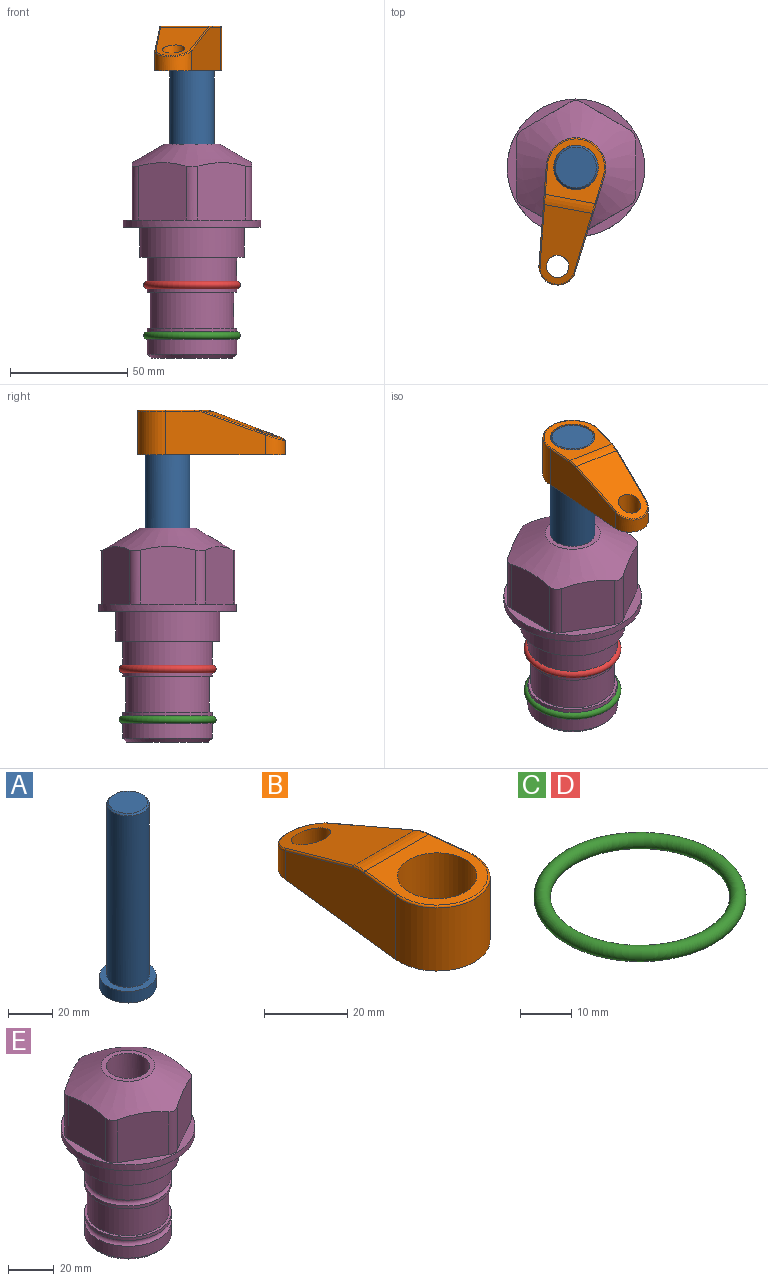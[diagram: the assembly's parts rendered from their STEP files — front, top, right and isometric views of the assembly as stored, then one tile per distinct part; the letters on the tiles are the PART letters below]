
ASSEMBLY  parts=5 mates=3
PART A: 6 faces, bbox 25.4x25.4x101.6 mm
  f0: plane 17.46x17.46mm, normal (0,0,1), area 239.5mm2, adj f5
  f1: plane 25.4x25.4mm, normal (0,0,-1), area 506.7mm2, adj f2
  f2: cylinder r=12.7mm len=25.4mm, axis (0,0,1), area 506.7mm2, adj f1,f3
  f3: plane 25.4x25.4mm, normal (0,0,1), area 221.7mm2, adj f2,f4
  f4: cylinder r=9.53mm len=94.46mm, axis (0,0,1), area 5653mm2, adj f3,f5
  f5: cone r=8.73mm half-angle=45deg, axis (0,0,-1), area 64.4mm2, adj f0,f4
PART B: 44 faces, bbox 27.5x64.5x19.1 mm
  f0: plane 2.3x0.95mm, normal (0,0,-1), area 1mm2, adj f25,f30,f34
  f1: plane 63.5x25.4mm, normal (0,0,-1), area 561.7mm2, adj f2,f3,f4,f5,f6,f7,f19,f20
  f2: cylinder r=12.7mm len=25.4mm, axis (0,0,-1), area 792.2mm2, adj f1,f3,f5,f13
  f3: plane 42.33x18.54mm, normal (0.99,0.11,0), area 647mm2, adj f1,f2,f4,f11,f12,f14
  f4: cylinder r=7.94mm len=15.78mm, axis (0,0,-1), area 158.6mm2, adj f1,f3,f5,f16
  f5: plane 42.33x18.54mm, normal (-0.99,0.11,0), area 647mm2, adj f1,f2,f4,f15,f17,f18
  f6: cylinder r=9.53mm len=19.05mm, axis (0,0,-1), area 1140.1mm2, adj f1,f8
  f7: cylinder r=4.76mm len=10.98mm, axis (0,0,-1), area 276.1mm2, adj f1,f9
  f8: plane 25.83x24.38mm, normal (0,0,1), area 262.2mm2, adj f6,f10,f11,f13,f15
  f9: plane 32.49x20.55mm, normal (0,0.34,0.94), area 489.9mm2, adj f7,f10,f14,f16,f18
  f10: cylinder r=12.7mm len=21.49mm, axis (-1,0,0), area 93.2mm2, adj f8,f9,f12,f17
  f11: cylinder r=0.51mm len=12.34mm, axis (0.11,-0.99,0), area 9.9mm2, adj f3,f8,f12,f13
  f12: bspline ~7.62x1.64mm, area 3.5mm2, adj f3,f10,f11,f14
  f13: torus R=12.19mm, axis (0,0,1), area 33.6mm2, adj f2,f8,f11,f15
  f14: cylinder r=0.51mm len=26.01mm, axis (0.1,-0.93,0.34), area 21.6mm2, adj f3,f9,f12,f16
  f15: cylinder r=0.51mm len=12.34mm, axis (0.11,0.99,0), area 9.9mm2, adj f5,f8,f13,f17
  f16: bspline ~15.78x7.05mm, area 15.7mm2, adj f4,f9,f14,f18
  f17: bspline ~7.62x1.64mm, area 3.5mm2, adj f5,f10,f15,f18
  f18: cylinder r=0.51mm len=26.01mm, axis (0.1,0.93,-0.34), area 21.6mm2, adj f5,f9,f16,f17
  f19: plane 21.6x14.29mm, normal (-0.99,-0.11,0), area 242.6mm2, adj f1,f26,f28,f34,f36,f38
  f20: plane 21.6x14.29mm, normal (0.99,-0.11,0), area 242.6mm2, adj f1,f27,f29,f37,f39,f41
  f21: cylinder r=12.7mm len=14.29mm, axis (0,0,-1), area 173.2mm2, adj f1,f26,f27,f30,f31,f33
  f22: cylinder r=7.94mm len=7.63mm, axis (0,0,-1), area 53.8mm2, adj f1,f28,f29,f42
  f23: plane 2.3x0.95mm, normal (0,0,-1), area 1mm2, adj f25,f33,f37
  f24: plane 17.94x12.32mm, normal (0,-0.34,-0.94), area 191.2mm2, adj f25,f38,f41,f42
  f25: cylinder r=9.53mm len=12.93mm, axis (-1,0,0), area 37.5mm2, adj f0,f23,f24,f31,f36,f39
  f26: cylinder r=1.59mm len=14.29mm, axis (0,0,-1), area 49mm2, adj f1,f19,f21,f32
  f27: cylinder r=1.59mm len=14.29mm, axis (0,0,-1), area 49mm2, adj f1,f20,f21,f35
  f28: cylinder r=1.59mm len=7.28mm, axis (0,0,-1), area 22.1mm2, adj f1,f19,f22,f40
  f29: cylinder r=1.59mm len=7.28mm, axis (0,0,-1), area 22.1mm2, adj f1,f20,f22,f43
  f30: torus R=14.29mm, axis (0,0,1), area 5.8mm2, adj f0,f21,f31,f32
  f31: bspline ~11.06x2.73mm, area 20.8mm2, adj f21,f25,f30,f33
  f32: sphere r=1.59mm, area 5.4mm2, adj f26,f30,f34
  f33: torus R=14.29mm, axis (0,0,1), area 5.8mm2, adj f21,f23,f31,f35
  f34: cylinder r=1.59mm len=1.68mm, axis (-0.11,0.99,0), area 2.4mm2, adj f0,f19,f32,f36
  f35: sphere r=1.59mm, area 5.4mm2, adj f27,f33,f37
  f36: bspline ~5.82x2.33mm, area 7.7mm2, adj f19,f25,f34,f38
  f37: cylinder r=1.59mm len=1.68mm, axis (0.11,0.99,0), area 2.4mm2, adj f20,f23,f35,f39
  f38: cylinder r=1.59mm len=18.33mm, axis (0.1,-0.93,0.34), area 46.7mm2, adj f19,f24,f36,f40
  f39: bspline ~5.82x2.33mm, area 7.7mm2, adj f20,f25,f37,f41
  f40: sphere r=1.59mm, area 3.6mm2, adj f28,f38,f42
  f41: cylinder r=1.59mm len=18.33mm, axis (0.1,0.93,-0.34), area 46.7mm2, adj f20,f24,f39,f43
  f42: bspline ~8.31x1.84mm, area 15.3mm2, adj f22,f24,f40,f43
  f43: sphere r=1.59mm, area 3.6mm2, adj f29,f41,f42
PART C: 1 faces, bbox 44.7x44.7x3.2 mm
  f0: torus R=19.05mm, axis (0,0,1), area 1193.9mm2
PART D: same geometry as C
PART E: 36 faces, bbox 58.7x58.7x91.2 mm
  f0: cylinder r=17.78mm len=35.56mm, axis (0,0,1), area 1670.8mm2, adj f23,f24,f31
  f1: cylinder r=19.05mm len=38.1mm, axis (0,0,1), area 1191.9mm2, adj f26,f27,f30
  f2: plane 58.66x58.66mm, normal (0,0,-1), area 1150.6mm2, adj f3,f28
  f3: cylinder r=29.33mm len=58.66mm, axis (0,0,-1), area 585.1mm2, adj f2,f4
  f4: plane 58.66x58.66mm, normal (0,0,1), area 475.9mm2, adj f3,f5,f6,f7,f8,f9,f10,f11
  f5: plane 24.5x20.32mm, normal (-0.5,0.87,0), area 562.8mm2, adj f4,f15,f16,f17
  f6: plane 24.5x20.32mm, normal (0.5,0.87,0), area 562.8mm2, adj f4,f14,f15,f17
  f7: plane 24.5x23.48mm, normal (1,0,0), area 562.8mm2, adj f4,f13,f14,f17
  f8: plane 24.5x20.32mm, normal (0.5,-0.87,0), area 562.8mm2, adj f4,f12,f13,f17
  f9: plane 24.5x20.32mm, normal (-0.5,-0.87,0), area 562.8mm2, adj f4,f11,f12,f17
  f10: plane 24.5x23.48mm, normal (-1,0,0), area 562.8mm2, adj f4,f11,f16,f17
  f11: cylinder r=5.08mm len=23.01mm, axis (0,0,-1), area 121.2mm2, adj f4,f9,f10,f17
  f12: cylinder r=5.08mm len=23.01mm, axis (0,0,-1), area 121.2mm2, adj f4,f8,f9,f17
  f13: cylinder r=5.08mm len=23.01mm, axis (0,0,-1), area 121.2mm2, adj f4,f7,f8,f17
  f14: cylinder r=5.08mm len=23.01mm, axis (0,0,-1), area 121.2mm2, adj f4,f6,f7,f17
  f15: cylinder r=5.08mm len=23.01mm, axis (0,0,-1), area 121.2mm2, adj f4,f5,f6,f17
  f16: cylinder r=5.08mm len=23.01mm, axis (0,0,-1), area 121.2mm2, adj f4,f5,f10,f17
  f17: cone r=11.73mm half-angle=60deg, axis (0,0,-1), area 2071.8mm2, adj f5,f6,f7,f8,f9,f10,f11,f12
  f18: plane 23.46x23.46mm, normal (0,0,1), area 147.4mm2, adj f17,f35
  f19: plane 34.93x34.93mm, normal (0,0,-1), area 958mm2, adj f29
  f20: cylinder r=19.05mm len=38.1mm, axis (0,0,1), area 760.1mm2, adj f21,f29
  f21: torus R=19.05mm, axis (0,0,1), area 565.3mm2, adj f20,f22
  f22: cylinder r=19.05mm len=38.1mm, axis (0,0,1), area 190mm2, adj f21,f23
  f23: plane 38.1x38.1mm, normal (0,0,1), area 146.9mm2, adj f0,f22
  f24: plane 38.1x38.1mm, normal (0,0,-1), area 146.9mm2, adj f0,f25
  f25: cylinder r=19.05mm len=38.1mm, axis (0,0,1), area 190mm2, adj f24,f26
  f26: torus R=19.05mm, axis (0,0,1), area 565.3mm2, adj f1,f25
  f27: plane 44.45x44.45mm, normal (0,0,-1), area 411.7mm2, adj f1,f28
  f28: cylinder r=22.23mm len=44.45mm, axis (0,0,1), area 1773.5mm2, adj f2,f27
  f29: cone r=19.05mm half-angle=45deg, axis (0,0,1), area 257.5mm2, adj f19,f20
  f30: cylinder r=3.17mm len=6.75mm, axis (-1,0,0), area 128mm2, adj f1,f33
  f31: cylinder r=3.17mm len=6.35mm, axis (-1,0,0), area 102.5mm2, adj f0,f33
  f32: plane 25.4x25.4mm, normal (0,0,1), area 506.7mm2, adj f33
  f33: cylinder r=12.7mm len=66.42mm, axis (0,0,-1), area 5236.2mm2, adj f30,f31,f32,f34
  f34: cone r=9.53mm half-angle=30deg, axis (0,0,-1), area 443.4mm2, adj f33,f35
  f35: cylinder r=9.53mm len=19.05mm, axis (0,0,-1), area 849mm2, adj f18,f34
PLACE A rot(axis=(0,0,-1),100.6deg) t=(0,0,12.22)mm
PLACE B rot(axis=(0,0,1),169.4deg) t=(0,0,66.83)mm
PLACE C t=(0,0,-21.59)mm
PLACE D at identity
PLACE E at identity fixed
MATE fastened C.f0 <-> E.f0  axis (0,0,1) through (0,0,-46.1)mm
MATE cylindrical A.f2 <-> E.f0  axis (0,0,1) through (0,0,37.86)mm
MATE fastened B.f2 <-> A.f2  axis (0,0,1) through (0,0,85.88)mm
